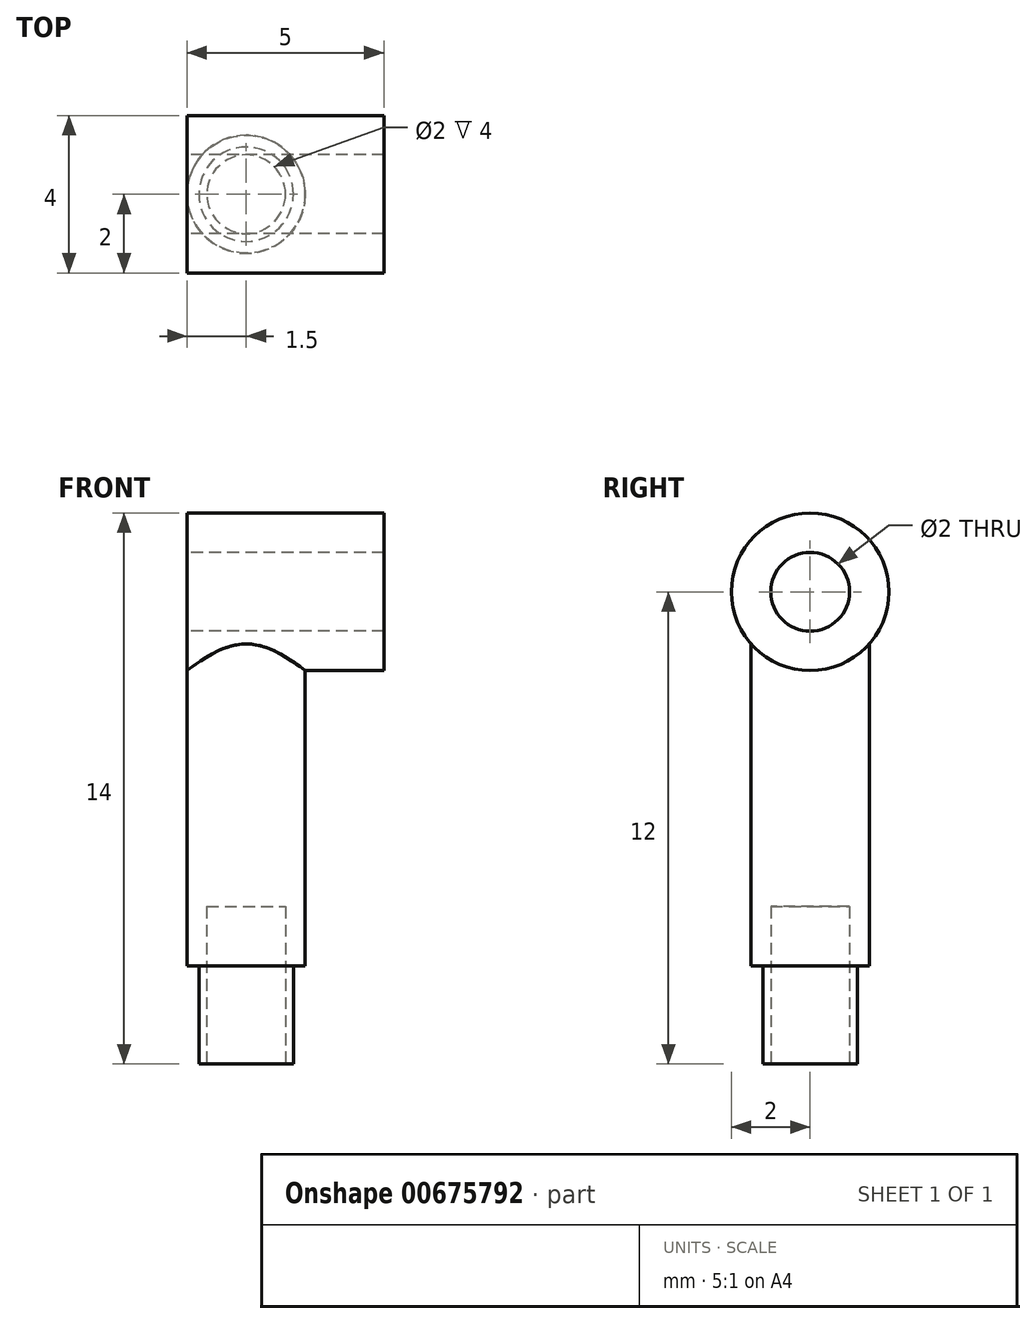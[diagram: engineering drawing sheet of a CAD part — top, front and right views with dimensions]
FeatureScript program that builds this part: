
annotation { "Feature Type Name" : "Feature", "Feature Type Description" : "" }
export const myFeature = defineFeature(function(context is Context, id is Id, definition is map)
    precondition{}
    {
        {
            var Q0;
            Q0=qCreatedBy(makeId("Front.planeOp"),FACE);
            var sketch = newSketch(context, id + "F0", { "sketchPlane" : qUnion([Q0])});
            skLineSegment(sketch, "E0", {"start": v(-3.12, -45.45) * mm, "end": v(-3.12, -45.45) * mm});
            skLineSegment(sketch, "E1", {"start": v(0, 0) * mm, "end": v(0, 1) * mm});
            skLineSegment(sketch, "E2", {"start": v(-5, 1) * mm, "end": v(-5, 0) * mm});
            skLineSegment(sketch, "E3", {"start": v(-5, 1) * mm, "end": v(0, 1) * mm});
            skLineSegment(sketch, "E4.MirrorCS", {"start": v(-1.5, 2) * mm, "end": v(0.83, 2) * mm});
            skLineSegment(sketch, "E5", {"start": v(0, 1) * mm, "end": v(0, 2) * mm});
            skLineSegment(sketch, "E6", {"start": v(-5, 0) * mm, "end": v(-5, -10) * mm});
            skLineSegment(sketch, "E7", {"start": v(-3.5, 0) * mm, "end": v(-3.5, -10) * mm});
            skLineSegment(sketch, "E8", {"start": v(-5, 0) * mm, "end": v(0, 0) * mm});
            skLineSegment(sketch, "E9", {"start": v(-5, -10) * mm, "end": v(-3.5, -10) * mm});
            skSolve(sketch);
        }
        {
            var Q0;
            {var subQ3=sQuery(id+"F0.wireOp",EDGE,"E1");Q0=makeQuery(id+"F0.imprint","IMPRINT",FACE,{"disambiguationData":[TD([[makeQuery(id+"F0.imprint","IMPRINT",EDGE,{"derivedFrom":subQ3}),1.0]])]});}
            var Q1;
            Q1=sQuery(id+"F0.wireOp",EDGE,"E4.MirrorCS");
            revolve(context, id + "F1", {"entities" : qUnion([Q0]), "axis" : qUnion([Q1]), "revolveType" : RevolveType.FULL});
        }
        {
            var Q0;
            {var subQ0=sQuery(id+"F0.wireOp",EDGE,"E6");Q0=makeQuery(id+"F0.imprint","IMPRINT",FACE,{"disambiguationData":[TD([[makeQuery(id+"F0.imprint","IMPRINT",EDGE,{"derivedFrom":subQ0}),1.0]])]});}
            var Q1;
            Q1=sQuery(id+"F0.wireOp",EDGE,"E7");
            revolve(context, id + "F2", {"operationType" : NewBodyOperationType.ADD, "entities" : qUnion([Q0]), "axis" : qUnion([Q1]), "revolveType" : RevolveType.FULL});
        }
        {
            var Q0;
            Q0=makeQuery(id+"F2.opRevolve","SWEPT_FACE",FACE,{"disambiguationData":[OSD([sQuery(id+"F0.wireOp",EDGE,"E8")])]});
            extrude(context, id + "F3", {"entities" : qUnion([Q0]), "operationType" : NewBodyOperationType.ADD, "depth" : 1 * mm, "offsetDistance" : 25 * mm});
        }
        {
            var Q0;
            Q0=makeQuery(id+"F2.opRevolve","SWEPT_FACE",FACE,{"disambiguationData":[OSD([sQuery(id+"F0.wireOp",EDGE,"E9")])]});
            var sketch = newSketch(context, id + "F4", { "sketchPlane" : qUnion([Q0])});
            skCircle(sketch, "E10", {"center": v(-3.5, 0) * mm, "radius": 1.2 * mm});
            skCircle(sketch, "E11", {"center": v(-3.5, 0) * mm, "radius": 1.5 * mm});
            skCircle(sketch, "E12", {"center": v(-3.5, 0) * mm, "radius": 1 * mm});
            skSolve(sketch);
        }
        {
            var Q0;
            Q0=makeQuery(id+"F4.imprint","IMPRINT",FACE,{"disambiguationData":[TD([[makeQuery(id+"F4.imprint","IMPRINT",EDGE,{"derivedFrom":sQuery(id+"F4.wireOp",EDGE,"E10")}),-1.0]])]});
            extrude(context, id + "F5", {"entities" : qUnion([Q0]), "operationType" : NewBodyOperationType.REMOVE, "oppositeDirection" : true, "depth" : 2.5 * mm, "offsetDistance" : 25 * mm});
        }
        {
            var Q0;
            Q0=makeQuery(id+"F4.imprint","IMPRINT",FACE,{"disambiguationData":[TD([[makeQuery(id+"F4.imprint","IMPRINT",EDGE,{"derivedFrom":sQuery(id+"F4.wireOp",EDGE,"E12")}),1.0]])]});
            extrude(context, id + "F6", {"entities" : qUnion([Q0]), "operationType" : NewBodyOperationType.REMOVE, "oppositeDirection" : true, "depth" : 4 * mm, "offsetDistance" : 25 * mm});
        }
    });
